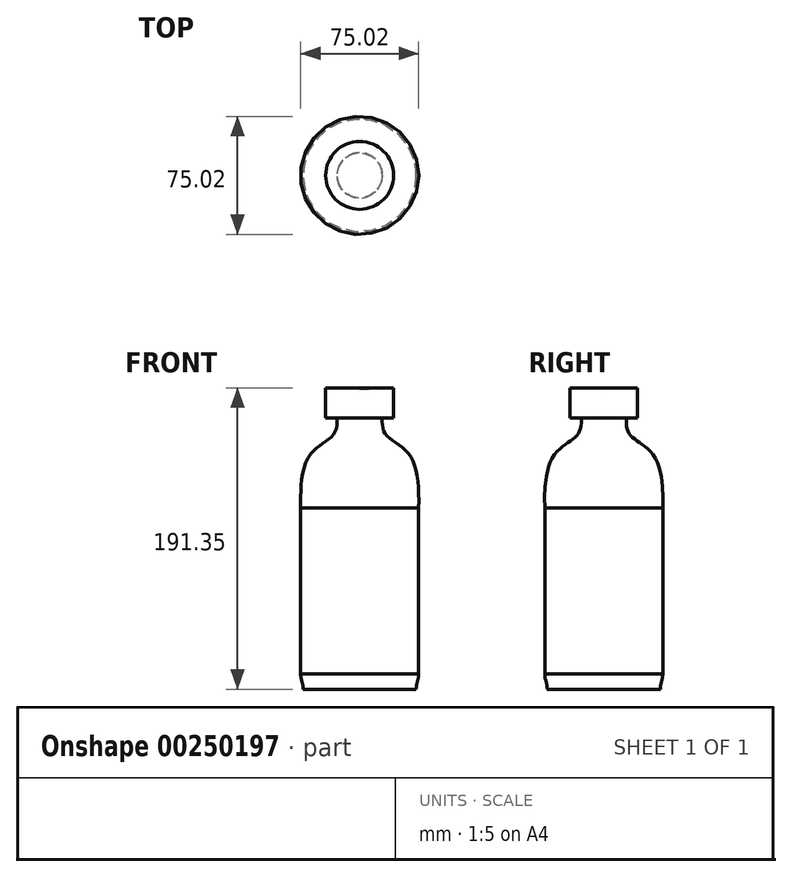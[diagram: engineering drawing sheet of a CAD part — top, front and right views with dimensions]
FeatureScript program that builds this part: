
annotation { "Feature Type Name" : "Feature", "Feature Type Description" : "" }
export const myFeature = defineFeature(function(context is Context, id is Id, definition is map)
    precondition{}
    {
        {
            var Q0;
            Q0=qCreatedBy(makeId("Front.planeOp"),FACE);
            var sketch = newSketch(context, id + "F0", { "sketchPlane" : qUnion([Q0])});
            skLineSegment(sketch, "E0", {"start": v(-37.46, 48.8) * mm, "end": v(-37.46, -45.7) * mm});
            skLineSegment(sketch, "E1", {"start": v(-35.92, -55.43) * mm, "end": v(0, -55.43) * mm});
            skLineSegment(sketch, "E2", {"start": v(0, -55.43) * mm, "end": v(0, 135.2) * mm, "construction": true});
            skLineSegment(sketch, "E3", {"start": v(-37.46, 48.8) * mm, "end": v(-37.46, 59.73) * mm});
            skLineSegment(sketch, "E4", {"start": v(0, 126.78) * mm, "end": v(0, -55.43) * mm});
            skFitSpline(sketch, "E5", {"points": [v(-37.46, 59.73) * mm, v(-30.79, 94.35) * mm, v(-16.97, 105.89) * mm, v(-14.36, 116.99) * mm], "startDerivative": vector(-2.37, 109.07) * mm, "endDerivative": vector(-3.34, 55.69) * mm});
            skLineSegment(sketch, "E6", {"start": v(-14.36, 116.99) * mm, "end": v(-21.54, 116.99) * mm});
            skLineSegment(sketch, "E7", {"start": v(-21.54, 116.99) * mm, "end": v(-21.54, 135.92) * mm});
            skLineSegment(sketch, "E8", {"start": v(-21.54, 135.92) * mm, "end": v(0, 135.2) * mm});
            skLineSegment(sketch, "E9", {"start": v(0, 135.2) * mm, "end": v(0, -55.43) * mm});
            skFitSpline(sketch, "E10", {"points": [v(-37.46, -45.7) * mm, v(-35.92, -55.43) * mm], "startDerivative": vector(-0.51, -9.81) * mm, "endDerivative": vector(-0.51, -9.81) * mm});
            skSolve(sketch);
        }
        {
            var Q0;
            Q0=makeQuery(id+"F0.imprint","IMPRINT",FACE,{"disambiguationData":[TD([[makeQuery(id+"F0.imprint","IMPRINT",EDGE,{"derivedFrom":sQuery(id+"F0.wireOp",EDGE,"E0")}),1.0]])]});
            var Q1;
            Q1=sQuery(id+"F0.wireOp",EDGE,"E4");
            revolve(context, id + "F1", {"entities" : qUnion([Q0]), "axis" : qUnion([Q1]), "revolveType" : RevolveType.FULL});
        }
    });
